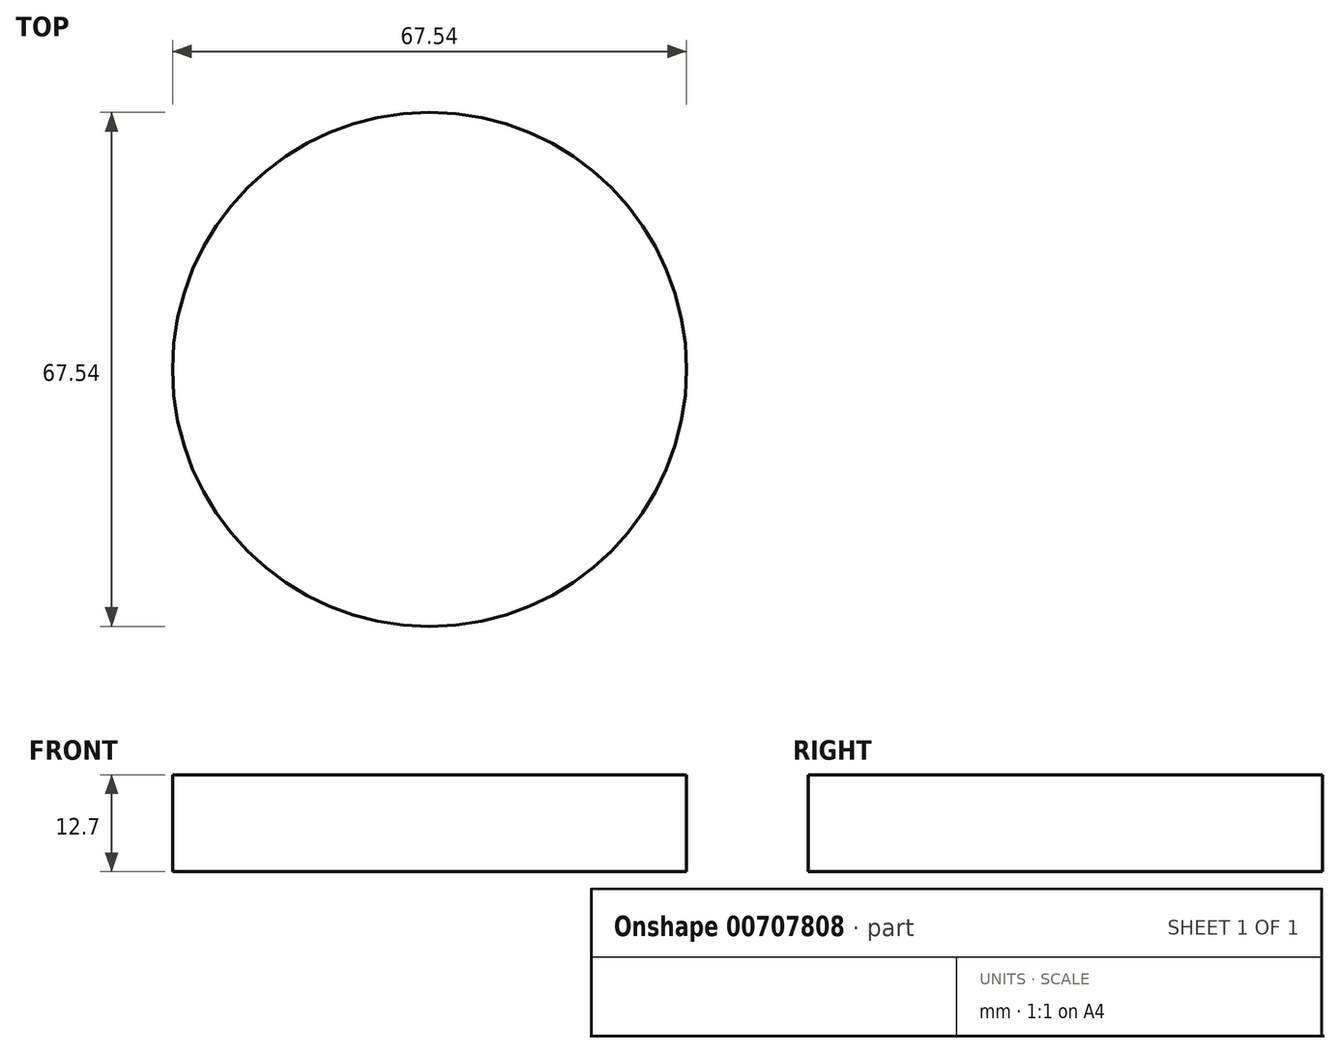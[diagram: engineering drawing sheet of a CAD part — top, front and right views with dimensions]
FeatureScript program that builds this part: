
annotation { "Feature Type Name" : "Feature", "Feature Type Description" : "" }
export const myFeature = defineFeature(function(context is Context, id is Id, definition is map)
    precondition{}
    {
        {
            var Q0;
            Q0=qCreatedBy(makeId("Top.planeOp"),FACE);
            var sketch = newSketch(context, id + "F0", { "sketchPlane" : qUnion([Q0])});
            skCircle(sketch, "E0", {"center": v(0, 0) * mm, "radius": 33.77 * mm});
            skSolve(sketch);
        }
        {
            var Q0;
            Q0=makeQuery(id+"F0.imprint","IMPRINT",FACE,{"disambiguationData":[TD([[makeQuery(id+"F0.imprint","IMPRINT",EDGE,{"derivedFrom":sQuery(id+"F0.wireOp",EDGE,"E0")}),1.0]])]});
            extrude(context, id + "F1", {"entities" : qUnion([Q0]), "oppositeDirection" : true, "depth" : 233.68 * mm, "offsetDistance" : 25.4 * mm});
        }
        {
            var Q0;
            Q0=makeQuery(id+"F1.opExtrude","CAP_FACE",FACE,{"disambiguationData":[OSD([sQuery(id+"F0.wireOp",EDGE,"E0")])],"isStart":true});
            extrude(context, id + "F2", {"entities" : qUnion([Q0]), "operationType" : NewBodyOperationType.REMOVE, "oppositeDirection" : true, "depth" : 231.14 * mm, "offsetDistance" : 25.4 * mm});
        }
        {
            var Q0;
            Q0=makeQuery(id+"F1.opExtrude","CAP_FACE",FACE,{"disambiguationData":[OSD([sQuery(id+"F0.wireOp",EDGE,"E0")])],"isStart":false});
            extrude(context, id + "F3", {"entities" : qUnion([Q0]), "operationType" : NewBodyOperationType.ADD, "depth" : 10.16 * mm, "offsetDistance" : 25.4 * mm});
        }
    });
